# Revit family: CCFLED-D2_AUA02211040101
name_source: partatom
category: Lighting Fixtures
units: mm (PartAtom-declared; Revit-internal decimal feet)

## family parameters
Cut with Voids When Loaded = No
Host = Face
Light Source = Yes
Part Type = Normal
Room Calculation Point = No
Round Connector Dimension = Use Diameter
Shared = No

## types (5) — shared parameters
Apparent Load = 3 VA
Clevertronics_AS2293 Classification = C0=D4 C90=E3.2
Clevertronics_Applicable Standards = AS/NZS3820, CISPR15, AS/NZS2293.3
Clevertronics_Battery = 3.2V 1500mAh
Clevertronics_Battery Type = Lithium Iron Phosphate
Clevertronics_Charger Method = Intelligent current limited constant voltage
Clevertronics_Construction = ABS Body and Diffuser with Polycarbonate Clear Tamper Proof Cover
Clevertronics_Diffuser = All directional inserts included in the box
Clevertronics_Dimensions Main Enclosure = 355mm x 80mm x 215mm
Clevertronics_Height = 215 mm
Clevertronics_IP Rating = IP20
Clevertronics_Length = 355 mm
Clevertronics_MIC Number = AUA02211040101
Clevertronics_Material = Clevertronics_Plastic
Clevertronics_Mounting = Wall, ceiling single-sided & ceiling double-sided
Clevertronics_Operating Mode = Maintained
Clevertronics_Operating Temperature = 1˚C to 40˚C
Clevertronics_Operating Voltage = 240V AC; 50Hz
Clevertronics_Power Consumption = 2.8 Watts (Standby), 4.1 Watts (Max)
Clevertronics_Product Description = Cleverfit Exit, Surface Mount, LP, DALI-2 Emergency, All Pictograms, Single or Double Sided
Clevertronics_Replacement Battery = Battery : 1550105
Clevertronics_Replacement Driver = Driver : 8002329
Clevertronics_Replacement Lamp = LED Strip : 8002710
Clevertronics_Testing Node = DALI-2 Node : 8003062
Clevertronics_Testing System = DALI-2
Clevertronics_Viewing Distance = 24m
Clevertronics_Weight = 1.6kg
Clevertronics_Width = 80 mm  [stored 0.262467 ft]
Color Filter = 16777215
Default Elevation = 1200 mm
Description = Cleverfit Exit, Surface Mount, LP, DALI-2 Emergency, All Pictograms, Single or Double Sided
Dimming Lamp Color Temperature Shift = <None>
Indication Right 'Face Two' = No
Lamp = 6 x LED, 100,000 hours
Manufacturer = Clevertronics
Model = CCFLED-D2
Photometric Web File = ll21444 -  CCFLED-ZW Gen2 .IES
Tilt Angle = -90.00°
zero-valued in all types: Clevertronics_Annotation Size

## per-type parameters (varying)
| type | Indication Left 'Face Two' | Indication Left 'Face one' | Indication Right 'Face one' | Runing Man common arrow | Straight line 'Face one' | Straight line 'Face two' | URL |
| Runing Man Single | No | No | No | No | Yes | No |  |
| Running Man Common arrow | Yes | No | No | Yes | No | No |  |
| Runing Man Right (Single) | No | No | Yes | No | No | No |  |
| Runing Man Double Sided | No | No | No | No | Yes | Yes | https://clevertronics.com.au |
| Runing Man Left (Single) | No | Yes | No | No | No | No |  |

note: [stored X ft] marks values corroborated as IEEE doubles in the binary element streams (Revit-internal decimal feet)

## geometry (parser evidence)
native form markers: Blend x2, Sweep x4
no freeform markers — native parametric forms only
